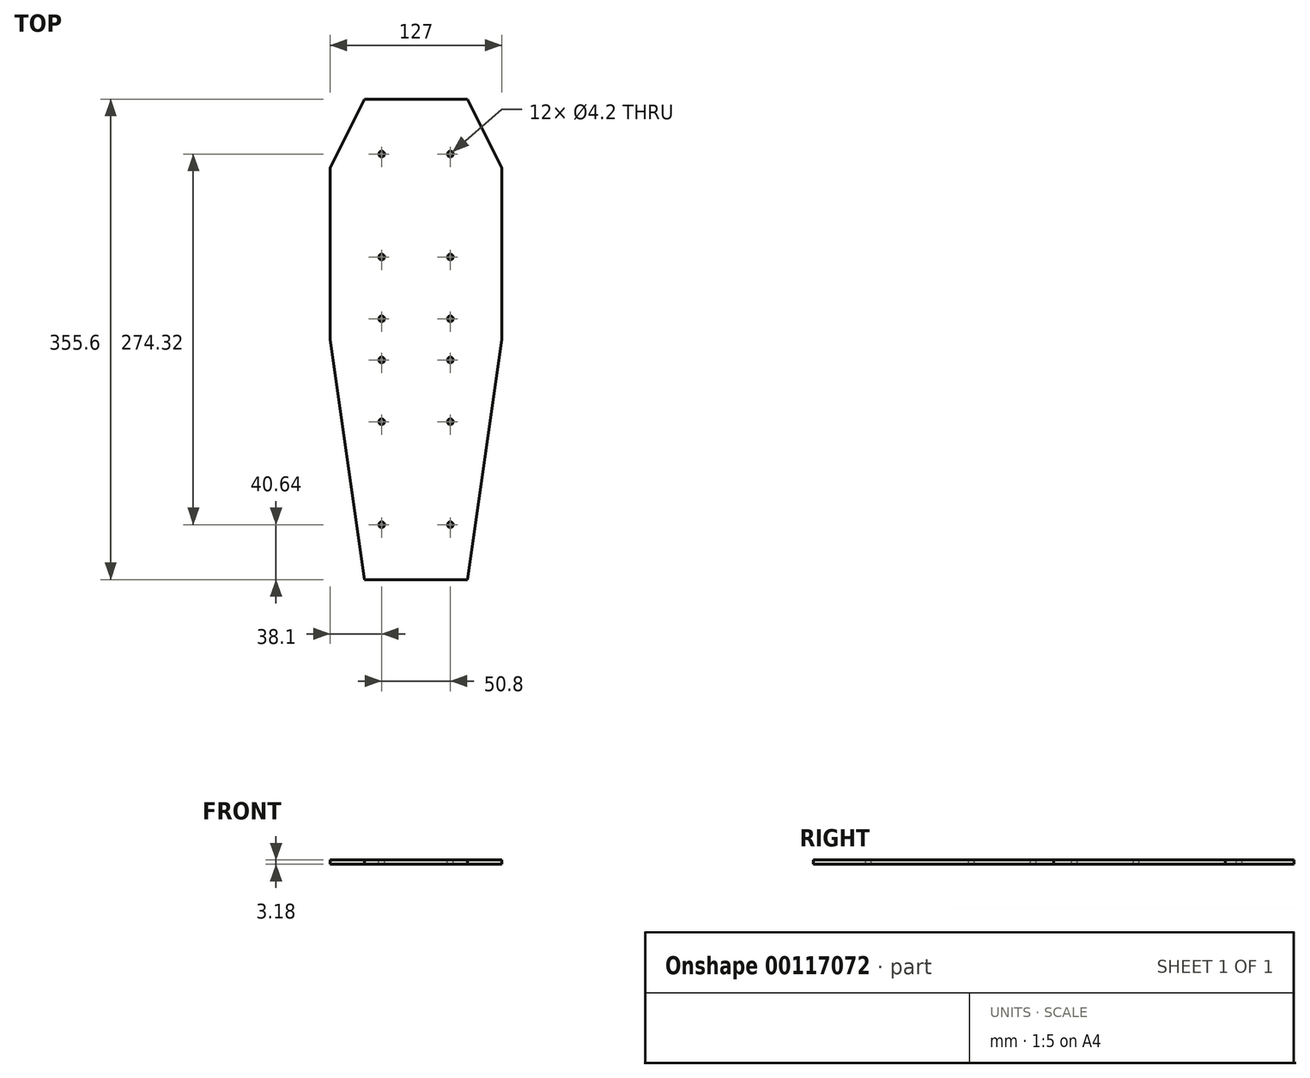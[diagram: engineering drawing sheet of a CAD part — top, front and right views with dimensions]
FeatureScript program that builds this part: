
annotation { "Feature Type Name" : "Feature", "Feature Type Description" : "" }
export const myFeature = defineFeature(function(context is Context, id is Id, definition is map)
    precondition{}
    {
        {
            var Q0;
            Q0=qCreatedBy(makeId("Top.planeOp"),FACE);
            var sketch = newSketch(context, id + "F0", { "sketchPlane" : qUnion([Q0])});
            skLineSegment(sketch, "E0", {"start": v(63.5, 0) * mm, "end": v(38.1, -177.8) * mm});
            skLineSegment(sketch, "E1.MirrorCS", {"start": v(-63.5, 0) * mm, "end": v(-38.1, -177.8) * mm});
            skLineSegment(sketch, "E2", {"start": v(38.1, -177.8) * mm, "end": v(-38.1, -177.8) * mm});
            skLineSegment(sketch, "E3", {"start": v(-63.5, 127) * mm, "end": v(-38.1, 177.8) * mm});
            skLineSegment(sketch, "E4.MirrorCS", {"start": v(63.5, 127) * mm, "end": v(38.1, 177.8) * mm});
            skLineSegment(sketch, "E5", {"start": v(-38.1, 177.8) * mm, "end": v(38.1, 177.8) * mm});
            skLineSegment(sketch, "E6", {"start": v(63.5, 127) * mm, "end": v(63.5, 0) * mm});
            skLineSegment(sketch, "E7", {"start": v(-63.5, 127) * mm, "end": v(-63.5, 0) * mm});
            skPoint(sketch, "E8", {"position": v(25.4, 141.48) * mm});
            skPoint(sketch, "E9", {"position": v(25.4, 62.74) * mm});
            skPoint(sketch, "E10", {"position": v(-25.4, 20.83) * mm});
            skPoint(sketch, "E11", {"position": v(25.4, 20.83) * mm});
            skPoint(sketch, "E12", {"position": v(29.21, -150.62) * mm});
            skPoint(sketch, "E13", {"position": v(-29.21, -150.62) * mm});
            skPoint(sketch, "E14", {"position": v(-25.4, 141.48) * mm});
            skPoint(sketch, "E15", {"position": v(-25.4, 62.74) * mm});
            skPoint(sketch, "E16", {"position": v(12.7, -74.42) * mm});
            skPoint(sketch, "E17", {"position": v(-12.7, -74.42) * mm});
            skSolve(sketch);
        }
        {
            var Q0;
            Q0=qSketchRegion(id+"F0",true);
            extrude(context, id + "F1", {"entities" : qUnion([Q0]), "depth" : 3.17 * mm});
        }
        {
            var Q0;
            Q0=makeQuery(id+"F1.opExtrude","CAP_FACE",FACE,{"disambiguationData":[OSD([sQuery(id+"F0.wireOp",EDGE,"E0"),sQuery(id+"F0.wireOp",EDGE,"E1.MirrorCS"),sQuery(id+"F0.wireOp",EDGE,"E2"),sQuery(id+"F0.wireOp",EDGE,"E3"),sQuery(id+"F0.wireOp",EDGE,"E4.MirrorCS"),sQuery(id+"F0.wireOp",EDGE,"E5"),sQuery(id+"F0.wireOp",EDGE,"E6"),sQuery(id+"F0.wireOp",EDGE,"E7")])],"isStart":false});
            var sketch = newSketch(context, id + "F2", { "sketchPlane" : qUnion([Q0])});
            skPoint(sketch, "E18", {"position": v(25.4, 137.16) * mm});
            skPoint(sketch, "E19", {"position": v(25.4, 60.96) * mm});
            skPoint(sketch, "E20", {"position": v(-25.4, 15.24) * mm});
            skPoint(sketch, "E21", {"position": v(25.4, 15.24) * mm});
            skPoint(sketch, "E22", {"position": v(25.4, -137.16) * mm});
            skPoint(sketch, "E23", {"position": v(-25.4, -137.16) * mm});
            skPoint(sketch, "E24", {"position": v(-25.4, 137.16) * mm});
            skPoint(sketch, "E25", {"position": v(-25.4, 60.96) * mm});
            skPoint(sketch, "E26", {"position": v(25.4, -60.96) * mm});
            skPoint(sketch, "E27", {"position": v(-25.4, -60.96) * mm});
            skPoint(sketch, "E28.MirrorP", {"position": v(-25.4, -15.24) * mm});
            skPoint(sketch, "E29.MirrorP", {"position": v(25.4, -15.24) * mm});
            skSolve(sketch);
        }
        {
            var Q0;
            Q0=sQuery(id+"F2.wireOp",VERTEX,"E24");
            var Q1;
            Q1=sQuery(id+"F2.wireOp",VERTEX,"E18");
            var Q2;
            Q2=sQuery(id+"F2.wireOp",VERTEX,"E19");
            var Q3;
            Q3=sQuery(id+"F2.wireOp",VERTEX,"E25");
            var Q4;
            Q4=sQuery(id+"F2.wireOp",VERTEX,"E20");
            var Q5;
            Q5=sQuery(id+"F2.wireOp",VERTEX,"E21");
            var Q6;
            Q6=sQuery(id+"F2.wireOp",VERTEX,"E26");
            var Q7;
            Q7=sQuery(id+"F2.wireOp",VERTEX,"E27");
            var Q8;
            Q8=sQuery(id+"F2.wireOp",VERTEX,"E23");
            var Q9;
            Q9=sQuery(id+"F2.wireOp",VERTEX,"E22");
            var Q10;
            Q10=sQuery(id+"F2.wireOp",VERTEX,"E28.MirrorP");
            var Q11;
            Q11=sQuery(id+"F2.wireOp",VERTEX,"E29.MirrorP");
            var Q12;
            Q12=makeQuery(id+"F1.opExtrude","SWEPT_BODY",BODY,{"disambiguationData":[OSD([sQuery(id+"F0.wireOp",EDGE,"E0"),sQuery(id+"F0.wireOp",EDGE,"E1.MirrorCS"),sQuery(id+"F0.wireOp",EDGE,"E2"),sQuery(id+"F0.wireOp",EDGE,"E3"),sQuery(id+"F0.wireOp",EDGE,"E4.MirrorCS"),sQuery(id+"F0.wireOp",EDGE,"E5"),sQuery(id+"F0.wireOp",EDGE,"E6"),sQuery(id+"F0.wireOp",EDGE,"E7")])]});
            hole(context, id + "F3", {"style" : HoleStyle.SIMPLE, "endStyle" : HoleEndStyle.THROUGH, "standardTappedOrClearance" : lookupTablePath({ "standard" : "ISO", "engagement" : "75%", "pitch" : "0.8 mm", "size" : "M5", "type" : "Tapped" }), "standardBlindInLast" : lookupTablePath({ "standard" : "ISO", "engagement" : "75%", "pitch" : "0.8 mm", "size" : "M5", "type" : "Tapped" }), "holeDiameter" : 4.2 * mm, "startFromSketch" : true, "locations" : qUnion([Q0, Q1, Q2, Q3, Q4, Q5, Q6, Q7, Q8, Q9, Q10, Q11]), "scope" : qUnion([Q12]), "isTappedThrough" : true, "majorDiameter" : 5 * mm, "showTappedDepth" : true});
        }
    });
